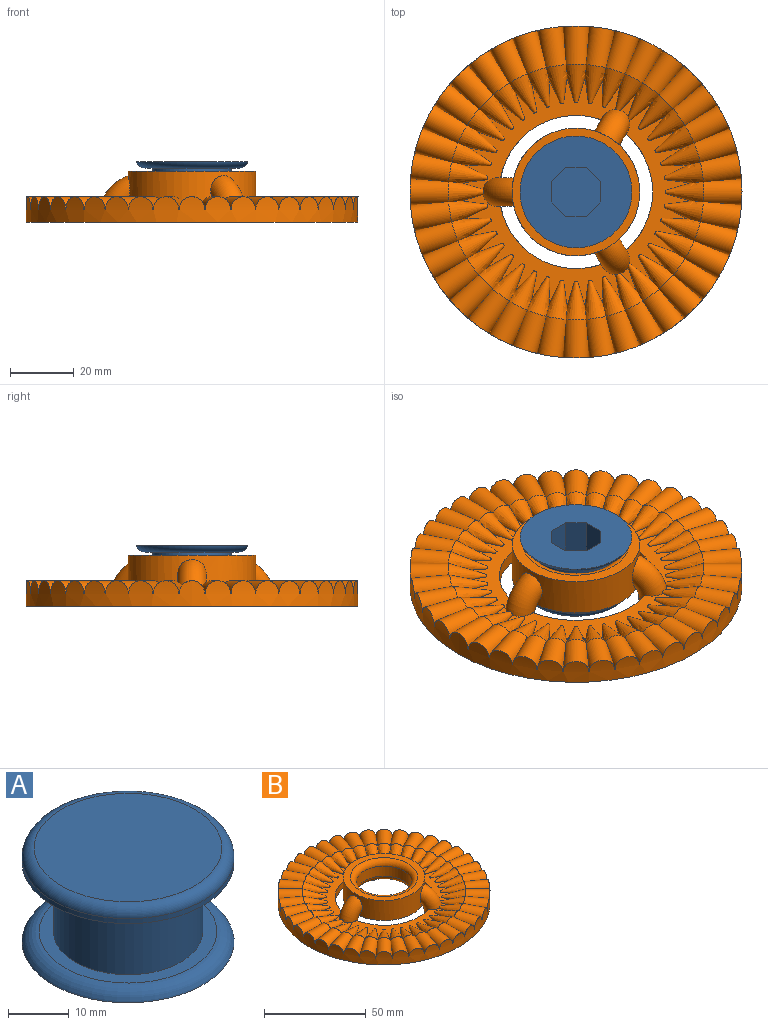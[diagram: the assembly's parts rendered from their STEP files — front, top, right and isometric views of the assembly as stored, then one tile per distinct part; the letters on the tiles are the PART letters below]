
ASSEMBLY  parts=2 mates=1
PART A: 17 faces, bbox 38.3x38.3x20 mm
  f0: plane 15x6.3mm, normal (-1,0,0), area 94.4mm2, adj f1,f7,f8,f16
  f1: plane 15x4.45mm, normal (-0.71,0.71,0), area 94.4mm2, adj f0,f2,f8,f16
  f2: plane 15x6.3mm, normal (0,1,0), area 94.4mm2, adj f1,f3,f8,f16
  f3: plane 15x4.45mm, normal (0.71,0.71,0), area 94.4mm2, adj f2,f4,f8,f16
  f4: plane 15x6.3mm, normal (1,0,0), area 94.4mm2, adj f3,f5,f8,f16
  f5: plane 15x4.45mm, normal (0.71,-0.71,0), area 94.4mm2, adj f4,f6,f8,f16
  f6: plane 15x6.3mm, normal (0,-1,0), area 94.4mm2, adj f5,f7,f8,f16
  f7: plane 15x4.45mm, normal (-0.71,-0.71,0), area 94.4mm2, adj f0,f6,f8,f16
  f8: plane 35x35mm, normal (0,0,-1), area 770.7mm2, adj f0,f1,f2,f3,f4,f5,f6,f7
  f9: plane 35x35mm, normal (0,0,-1), area 486.8mm2, adj f10,f14
  f10: cylinder r=12.3mm len=24.6mm, axis (0,0,-1), area 1082mm2, adj f9,f11
  f11: plane 29.34x29.34mm, normal (0,0,1), area 201mm2, adj f10,f15
  f12: plane 31x31mm, normal (0,0,1), area 754.8mm2, adj f13
  f13: torus R=15.5mm, axis (0,0,1), area 331.1mm2, adj f12,f14
  f14: cylinder r=17.5mm len=35mm, axis (0,0,1), area 110mm2, adj f9,f13
  f15: torus R=14.67mm, axis (0,0,-1), area 378.1mm2, adj f8,f11
  f16: plane 15.2x15.2mm, normal (0,0,-1), area 191.4mm2, adj f0,f1,f2,f3,f4,f5,f6,f7
PART B: 180 faces, bbox 20000000000000000038313501714693374724319102545303840223056070291987586484079775119224722902163606470656x20000000000000000038313501714693374724319102545303840223056070291987586484079775119224722902163606470656x16 mm
  f0: cylinder r=4mm len=13.1mm, axis (-0.16,0.99,0), area 111.7mm2, adj f1,f2,f175,f176,f177,f178
  f1: plane 1.02x0.16mm, normal (0,0,1), area 0.1mm2, adj f0,f2,f178
  f2: cylinder r=4mm len=12mm, axis (0,1,0), area 111.7mm2, adj f0,f1,f3,f4,f174,f178
  f3: plane 1.02x0.16mm, normal (0,0,1), area 0.1mm2, adj f2,f4,f178
  f4: cylinder r=4mm len=13.1mm, axis (0.16,0.99,0), area 111.7mm2, adj f2,f3,f5,f6,f173,f178
  f5: plane 1.01x0.32mm, normal (0,0,1), area 0.1mm2, adj f4,f6,f178
  f6: cylinder r=4mm len=13.89mm, axis (0.31,0.95,0), area 111.7mm2, adj f4,f5,f7,f8,f172,f178
  f7: plane 0.97x0.46mm, normal (0,0,1), area 0.1mm2, adj f6,f8,f178
  f8: cylinder r=4mm len=14.32mm, axis (0.45,0.89,0), area 111.7mm2, adj f6,f7,f9,f10,f171,f178
  f9: plane 0.91x0.6mm, normal (0,0,1), area 0.1mm2, adj f8,f10,f178
  f10: cylinder r=4mm len=14.41mm, axis (0.59,0.81,0), area 111.7mm2, adj f8,f9,f11,f12,f170,f178
  f11: plane 0.83x0.72mm, normal (0,0,1), area 0.1mm2, adj f10,f12,f178
  f12: cylinder r=4mm len=14.14mm, axis (0.71,0.71,0), area 111.7mm2, adj f10,f11,f13,f14,f169,f178
  f13: plane 0.83x0.72mm, normal (0,0,1), area 0.1mm2, adj f12,f14,f178
  f14: cylinder r=4mm len=14.41mm, axis (0.81,0.59,0), area 111.7mm2, adj f12,f13,f15,f16,f168,f178
  f15: plane 0.91x0.6mm, normal (0,0,1), area 0.1mm2, adj f14,f16,f178
  f16: cylinder r=4mm len=14.32mm, axis (0.89,0.45,0), area 111.7mm2, adj f14,f15,f17,f18,f167,f178
  f17: plane 0.97x0.46mm, normal (0,0,1), area 0.1mm2, adj f16,f18,f178
  f18: cylinder r=4mm len=13.89mm, axis (0.95,0.31,0), area 111.7mm2, adj f16,f17,f19,f20,f166,f178
  f19: plane 1.01x0.32mm, normal (0,0,1), area 0.1mm2, adj f18,f20,f178
  f20: cylinder r=4mm len=13.1mm, axis (0.99,0.16,0), area 111.7mm2, adj f18,f19,f21,f22,f165,f178
  f21: plane 1.02x0.16mm, normal (0,0,1), area 0.1mm2, adj f20,f22,f178
  f22: cylinder r=4mm len=12mm, axis (1,0,0), area 111.7mm2, adj f20,f21,f23,f24,f164,f178
  f23: plane 1.02x0.16mm, normal (0,0,1), area 0.1mm2, adj f22,f24,f178
  f24: cylinder r=4mm len=13.1mm, axis (0.99,-0.16,0), area 111.7mm2, adj f22,f23,f25,f26,f163,f178
  f25: plane 1.01x0.32mm, normal (0,0,1), area 0.1mm2, adj f24,f26,f178
  f26: cylinder r=4mm len=13.89mm, axis (0.95,-0.31,0), area 111.7mm2, adj f24,f25,f27,f28,f162,f178
  f27: plane 0.97x0.46mm, normal (0,0,1), area 0.1mm2, adj f26,f28,f178
  f28: cylinder r=4mm len=14.32mm, axis (0.89,-0.45,0), area 111.7mm2, adj f26,f27,f29,f30,f161,f178
  f29: plane 0.91x0.6mm, normal (0,0,1), area 0.1mm2, adj f28,f30,f178
  f30: cylinder r=4mm len=14.41mm, axis (0.81,-0.59,0), area 111.7mm2, adj f28,f29,f31,f32,f160,f178
  f31: plane 0.83x0.72mm, normal (0,0,1), area 0.1mm2, adj f30,f32,f178
  f32: cylinder r=4mm len=14.14mm, axis (0.71,-0.71,0), area 111.7mm2, adj f30,f31,f33,f34,f159,f178
  f33: plane 0.83x0.72mm, normal (0,0,1), area 0.1mm2, adj f32,f34,f178
  f34: cylinder r=4mm len=14.41mm, axis (0.59,-0.81,0), area 111.7mm2, adj f32,f33,f35,f36,f158,f178
  f35: plane 0.91x0.6mm, normal (0,0,1), area 0.1mm2, adj f34,f36,f178
  f36: cylinder r=4mm len=14.32mm, axis (0.45,-0.89,0), area 111.7mm2, adj f34,f35,f37,f38,f157,f178
  f37: plane 0.97x0.46mm, normal (0,0,1), area 0.1mm2, adj f36,f38,f178
  f38: cylinder r=4mm len=13.89mm, axis (0.31,-0.95,0), area 111.7mm2, adj f36,f37,f39,f40,f156,f178
  f39: plane 1.01x0.32mm, normal (0,0,1), area 0.1mm2, adj f38,f40,f178
  f40: cylinder r=4mm len=13.1mm, axis (0.16,-0.99,0), area 111.7mm2, adj f38,f39,f41,f42,f155,f178
  f41: plane 1.02x0.16mm, normal (0,0,1), area 0.1mm2, adj f40,f42,f178
  f42: cylinder r=4mm len=12mm, axis (0,-1,0), area 111.7mm2, adj f40,f41,f43,f44,f154,f178
  f43: plane 1.02x0.16mm, normal (0,0,1), area 0.1mm2, adj f42,f44,f178
  f44: cylinder r=4mm len=13.1mm, axis (-0.16,-0.99,0), area 111.7mm2, adj f42,f43,f45,f46,f153,f178
  f45: plane 1.01x0.32mm, normal (0,0,1), area 0.1mm2, adj f44,f46,f178
  f46: cylinder r=4mm len=13.89mm, axis (-0.31,-0.95,0), area 111.7mm2, adj f44,f45,f47,f48,f152,f178
  f47: plane 0.97x0.46mm, normal (0,0,1), area 0.1mm2, adj f46,f48,f178
  f48: cylinder r=4mm len=14.32mm, axis (-0.45,-0.89,0), area 111.7mm2, adj f46,f47,f49,f50,f151,f178
  f49: plane 0.91x0.6mm, normal (0,0,1), area 0.1mm2, adj f48,f50,f178
  f50: cylinder r=4mm len=14.41mm, axis (-0.59,-0.81,0), area 111.7mm2, adj f48,f49,f51,f52,f150,f178
  f51: plane 0.83x0.72mm, normal (0,0,1), area 0.1mm2, adj f50,f52,f178
  f52: cylinder r=4mm len=14.14mm, axis (-0.71,-0.71,0), area 111.7mm2, adj f50,f51,f53,f54,f149,f178
  f53: plane 0.83x0.72mm, normal (0,0,1), area 0.1mm2, adj f52,f54,f178
  f54: cylinder r=4mm len=14.41mm, axis (-0.81,-0.59,0), area 111.7mm2, adj f52,f53,f55,f56,f148,f178
  f55: plane 0.91x0.6mm, normal (0,0,1), area 0.1mm2, adj f54,f56,f178
  f56: cylinder r=4mm len=14.32mm, axis (-0.89,-0.45,0), area 111.7mm2, adj f54,f55,f57,f58,f147,f178
  f57: plane 0.97x0.46mm, normal (0,0,1), area 0.1mm2, adj f56,f58,f178
  f58: cylinder r=4mm len=13.89mm, axis (-0.95,-0.31,0), area 111.7mm2, adj f56,f57,f59,f60,f146,f178
  f59: plane 1.01x0.32mm, normal (0,0,1), area 0.1mm2, adj f58,f60,f178
  f60: cylinder r=4mm len=13.1mm, axis (-0.99,-0.16,0), area 111.7mm2, adj f58,f59,f61,f62,f145,f178
  f61: plane 1.02x0.16mm, normal (0,0,1), area 0.1mm2, adj f60,f62,f178
  f62: cylinder r=4mm len=12mm, axis (-1,0,0), area 111.7mm2, adj f60,f61,f63,f64,f144,f178
  f63: plane 1.02x0.16mm, normal (0,0,1), area 0.1mm2, adj f62,f64,f178
  f64: cylinder r=4mm len=13.1mm, axis (-0.99,0.16,0), area 111.7mm2, adj f62,f63,f65,f66,f143,f178
  f65: plane 1.01x0.32mm, normal (0,0,1), area 0.1mm2, adj f64,f66,f178
  f66: cylinder r=4mm len=13.89mm, axis (-0.95,0.31,0), area 111.7mm2, adj f64,f65,f67,f68,f142,f178
  f67: plane 0.97x0.46mm, normal (0,0,1), area 0.1mm2, adj f66,f68,f178
  f68: cylinder r=4mm len=14.32mm, axis (-0.89,0.45,0), area 111.7mm2, adj f66,f67,f69,f70,f141,f178
  f69: plane 0.91x0.6mm, normal (0,0,1), area 0.1mm2, adj f68,f70,f178
  f70: cylinder r=4mm len=14.41mm, axis (-0.81,0.59,0), area 111.7mm2, adj f68,f69,f71,f72,f140,f178
  f71: plane 0.83x0.72mm, normal (0,0,1), area 0.1mm2, adj f70,f72,f178
  f72: cylinder r=4mm len=14.14mm, axis (-0.71,0.71,0), area 111.7mm2, adj f70,f71,f73,f74,f139,f178
  f73: plane 0.83x0.72mm, normal (0,0,1), area 0.1mm2, adj f72,f74,f178
  f74: cylinder r=4mm len=14.41mm, axis (-0.59,0.81,0), area 111.7mm2, adj f72,f73,f75,f76,f138,f178
  f75: plane 0.91x0.6mm, normal (0,0,1), area 0.1mm2, adj f74,f76,f178
  f76: cylinder r=4mm len=14.32mm, axis (-0.45,0.89,0), area 111.7mm2, adj f74,f75,f77,f78,f176,f178
  f77: plane 0.97x0.46mm, normal (0,0,1), area 0.1mm2, adj f76,f176,f178
  f78: cone r=0.5mm half-angle=16.3deg, axis (0.45,-0.89,0), area 72.9mm2, adj f76,f79,f81,f136,f137,f138
  f79: cone r=0.5mm half-angle=16.3deg, axis (0.31,-0.95,0), area 74.6mm2, adj f78,f80,f81,f175,f176
  f80: plane 0.95x0.5mm, normal (-0.31,0.95,0), area 0.4mm2, adj f79,f81
  f81: plane 49.82x35.18mm, normal (0,0,1), area 360.6mm2, adj f78,f79,f80,f82,f124,f125,f126,f127
  f82: torus R=10mm, axis (0,1,0), area 250mm2, adj f81,f83,f108,f121,f122,f123,f124,f164
  f83: plane 40x39.94mm, normal (0,0,-1), area 398.9mm2, adj f82,f84,f104,f123,f136
  f84: torus R=10mm, axis (0.87,-0.5,0), area 244mm2, adj f83,f85,f86,f87,f100,f103,f108,f121
  f85: plane 7.24x4.91mm, normal (0,0,1), area 10.4mm2, adj f84,f150,f151
  f86: plane 0.49x0.3mm, normal (-0.59,-0.81,0), area 0.1mm2, adj f84,f87,f150
  f87: plane 54.92x20.39mm, normal (0,0,1), area 349.2mm2, adj f84,f86,f88,f89,f90,f91,f92,f93
  f88: plane 0.71x0.71mm, normal (-0.71,-0.71,0), area 0.4mm2, adj f87,f149
  f89: plane 0.81x0.59mm, normal (-0.81,-0.59,0), area 0.4mm2, adj f87,f148
  f90: plane 0.89x0.5mm, normal (-0.89,-0.45,0), area 0.4mm2, adj f87,f147
  f91: plane 0.95x0.5mm, normal (-0.95,-0.31,0), area 0.4mm2, adj f87,f146
  f92: plane 0.99x0.5mm, normal (-0.99,-0.16,0), area 0.4mm2, adj f87,f145
  f93: plane 1x0.5mm, normal (-1,0,0), area 0.4mm2, adj f87,f144
  f94: plane 0.99x0.5mm, normal (-0.99,0.16,0), area 0.4mm2, adj f87,f143
  f95: plane 0.95x0.5mm, normal (-0.95,0.31,0), area 0.4mm2, adj f87,f142
  f96: plane 0.89x0.5mm, normal (-0.89,0.45,0), area 0.4mm2, adj f87,f141
  f97: plane 0.81x0.59mm, normal (-0.81,0.59,0), area 0.4mm2, adj f87,f140
  f98: plane 0.71x0.71mm, normal (-0.71,0.71,0), area 0.4mm2, adj f87,f139
  f99: plane 0.49x0.3mm, normal (-0.59,0.81,0), area 0.1mm2, adj f87,f136,f138
  f100: cylinder r=24mm len=36.62mm, axis (0,0,-1), area 166.2mm2, adj f84,f87,f101,f102,f103,f136
  f101: plane 104x104mm, normal (0,0,-1), area 6750.5mm2, adj f100,f102,f103,f121,f122,f124,f178
  f102: cylinder r=4.5mm len=7.52mm, axis (0,0,1), area 11.3mm2, adj f100,f101,f124,f136
  f103: cylinder r=4.5mm len=7.52mm, axis (0,0,1), area 11.3mm2, adj f84,f100,f101,f121
  f104: torus R=16.5mm, axis (0,0,1), area 432mm2, adj f83,f105
  f105: cylinder r=13.5mm len=27mm, axis (0,0,-1), area 508.9mm2, adj f104,f106
  f106: torus R=16.5mm, axis (0,0,1), area 432mm2, adj f105,f107
  f107: plane 40x40mm, normal (0,0,1), area 401.3mm2, adj f106,f123
  f108: plane 49.82x35.18mm, normal (0,0,1), area 360.6mm2, adj f82,f84,f109,f110,f111,f112,f113,f114
  f109: plane 0.99x0.5mm, normal (0.99,-0.16,0), area 0.4mm2, adj f108,f163
  f110: plane 0.95x0.5mm, normal (0.95,-0.31,0), area 0.4mm2, adj f108,f162
  f111: plane 0.89x0.5mm, normal (0.89,-0.45,0), area 0.4mm2, adj f108,f161
  f112: plane 0.81x0.59mm, normal (0.81,-0.59,0), area 0.4mm2, adj f108,f160
  f113: plane 0.71x0.71mm, normal (0.71,-0.71,0), area 0.4mm2, adj f108,f159
  f114: plane 0.81x0.59mm, normal (0.59,-0.81,0), area 0.4mm2, adj f108,f158
  f115: plane 0.89x0.5mm, normal (0.45,-0.89,0), area 0.4mm2, adj f108,f157
  f116: plane 0.95x0.5mm, normal (0.31,-0.95,0), area 0.4mm2, adj f108,f156
  f117: plane 0.99x0.5mm, normal (0.16,-0.99,0), area 0.4mm2, adj f108,f155
  f118: plane 1x0.5mm, normal (0,-1,0), area 0.4mm2, adj f108,f154
  f119: plane 0.99x0.5mm, normal (-0.16,-0.99,0), area 0.4mm2, adj f108,f153
  f120: plane 0.95x0.5mm, normal (-0.31,-0.95,0), area 0.4mm2, adj f108,f152
  f121: cylinder r=24mm len=31.71mm, axis (0,0,-1), area 166.2mm2, adj f82,f84,f101,f103,f108,f122
  f122: cylinder r=4.5mm len=8.56mm, axis (0,0,1), area 11.3mm2, adj f82,f101,f121,f124
  f123: cylinder r=20mm len=40mm, axis (0,0,-1), area 1280.3mm2, adj f82,f83,f84,f107,f136
  f124: cylinder r=24mm len=31.71mm, axis (0,0,-1), area 166.2mm2, adj f81,f82,f101,f102,f122,f136
  f125: plane 0.99x0.5mm, normal (-0.16,0.99,0), area 0.4mm2, adj f81,f175
  f126: plane 1x0.5mm, normal (0,1,0), area 0.4mm2, adj f81,f174
  f127: plane 0.99x0.5mm, normal (0.16,0.99,0), area 0.4mm2, adj f81,f173
  f128: plane 0.95x0.5mm, normal (0.31,0.95,0), area 0.4mm2, adj f81,f172
  f129: plane 0.89x0.5mm, normal (0.45,0.89,0), area 0.4mm2, adj f81,f171
  f130: plane 0.81x0.59mm, normal (0.59,0.81,0), area 0.4mm2, adj f81,f170
  f131: plane 0.71x0.71mm, normal (0.71,0.71,0), area 0.4mm2, adj f81,f169
  f132: plane 0.81x0.59mm, normal (0.81,0.59,0), area 0.4mm2, adj f81,f168
  f133: plane 0.89x0.5mm, normal (0.89,0.45,0), area 0.4mm2, adj f81,f167
  f134: plane 0.95x0.5mm, normal (0.95,0.31,0), area 0.4mm2, adj f81,f166
  f135: plane 0.99x0.5mm, normal (0.99,0.16,0), area 0.4mm2, adj f81,f165
  f136: torus R=10mm, axis (-0.87,-0.5,0), area 249.6mm2, adj f78,f81,f83,f87,f99,f100,f102,f123
  f137: plane 7.24x4.91mm, normal (0,0,1), area 10.4mm2, adj f78,f136,f138
  f138: cone r=0.5mm half-angle=16.3deg, axis (0.59,-0.81,0), area 74.2mm2, adj f74,f78,f87,f99,f136,f137,f139
  f139: cone r=0.5mm half-angle=16.3deg, axis (0.71,-0.71,0), area 74.6mm2, adj f72,f87,f98,f138,f140
  f140: cone r=0.5mm half-angle=16.3deg, axis (0.81,-0.59,0), area 74.6mm2, adj f70,f87,f97,f139,f141
  f141: cone r=0.5mm half-angle=16.3deg, axis (0.89,-0.45,0), area 74.6mm2, adj f68,f87,f96,f140,f142
  f142: cone r=0.5mm half-angle=16.3deg, axis (0.95,-0.31,0), area 74.6mm2, adj f66,f87,f95,f141,f143
  f143: cone r=0.5mm half-angle=16.3deg, axis (0.99,-0.16,0), area 74.6mm2, adj f64,f87,f94,f142,f144
  f144: cone r=0.5mm half-angle=16.3deg, axis (1,0,0), area 74.6mm2, adj f62,f87,f93,f143,f145
  f145: cone r=0.5mm half-angle=16.3deg, axis (0.99,0.16,0), area 74.6mm2, adj f60,f87,f92,f144,f146
  f146: cone r=0.5mm half-angle=16.3deg, axis (0.95,0.31,0), area 74.6mm2, adj f58,f87,f91,f145,f147
  f147: cone r=0.5mm half-angle=16.3deg, axis (0.89,0.45,0), area 74.6mm2, adj f56,f87,f90,f146,f148
  f148: cone r=0.5mm half-angle=16.3deg, axis (0.81,0.59,0), area 74.6mm2, adj f54,f87,f89,f147,f149
  f149: cone r=0.5mm half-angle=16.3deg, axis (0.71,0.71,0), area 74.6mm2, adj f52,f87,f88,f148,f150
  f150: cone r=0.5mm half-angle=16.3deg, axis (0.59,0.81,0), area 74.2mm2, adj f50,f84,f85,f86,f87,f149,f151
  f151: cone r=0.5mm half-angle=16.3deg, axis (0.45,0.89,0), area 72.9mm2, adj f48,f84,f85,f108,f150,f152
  f152: cone r=0.5mm half-angle=16.3deg, axis (0.31,0.95,0), area 74.6mm2, adj f46,f108,f120,f151,f153
  f153: cone r=0.5mm half-angle=16.3deg, axis (0.16,0.99,0), area 74.6mm2, adj f44,f108,f119,f152,f154
  f154: cone r=0.5mm half-angle=16.3deg, axis (0,1,0), area 74.6mm2, adj f42,f108,f118,f153,f155
  f155: cone r=0.5mm half-angle=16.3deg, axis (-0.16,0.99,0), area 74.6mm2, adj f40,f108,f117,f154,f156
  f156: cone r=0.5mm half-angle=16.3deg, axis (-0.31,0.95,0), area 74.6mm2, adj f38,f108,f116,f155,f157
  f157: cone r=0.5mm half-angle=16.3deg, axis (-0.45,0.89,0), area 74.6mm2, adj f36,f108,f115,f156,f158
  f158: cone r=0.5mm half-angle=16.3deg, axis (-0.59,0.81,0), area 74.6mm2, adj f34,f108,f114,f157,f159
  f159: cone r=0.5mm half-angle=16.3deg, axis (-0.71,0.71,0), area 74.6mm2, adj f32,f108,f113,f158,f160
  f160: cone r=0.5mm half-angle=16.3deg, axis (-0.81,0.59,0), area 74.6mm2, adj f30,f108,f112,f159,f161
  f161: cone r=0.5mm half-angle=16.3deg, axis (-0.89,0.45,0), area 74.6mm2, adj f28,f108,f111,f160,f162
  f162: cone r=0.5mm half-angle=16.3deg, axis (-0.95,0.31,0), area 74.6mm2, adj f26,f108,f110,f161,f163
  f163: cone r=0.5mm half-angle=16.3deg, axis (-0.99,0.16,0), area 74.6mm2, adj f24,f108,f109,f162,f164
  f164: cone r=0.5mm half-angle=16.3deg, axis (-1,0,0), area 72.4mm2, adj f22,f81,f82,f108,f163,f165
  f165: cone r=0.5mm half-angle=16.3deg, axis (-0.99,-0.16,0), area 74.6mm2, adj f20,f81,f135,f164,f166
  f166: cone r=0.5mm half-angle=16.3deg, axis (-0.95,-0.31,0), area 74.6mm2, adj f18,f81,f134,f165,f167
  f167: cone r=0.5mm half-angle=16.3deg, axis (-0.89,-0.45,0), area 74.6mm2, adj f16,f81,f133,f166,f168
  f168: cone r=0.5mm half-angle=16.3deg, axis (-0.81,-0.59,0), area 74.6mm2, adj f14,f81,f132,f167,f169
  f169: cone r=0.5mm half-angle=16.3deg, axis (-0.71,-0.71,0), area 74.6mm2, adj f12,f81,f131,f168,f170
  f170: cone r=0.5mm half-angle=16.3deg, axis (-0.59,-0.81,0), area 74.6mm2, adj f10,f81,f130,f169,f171
  f171: cone r=0.5mm half-angle=16.3deg, axis (-0.45,-0.89,0), area 74.6mm2, adj f8,f81,f129,f170,f172
  f172: cone r=0.5mm half-angle=16.3deg, axis (-0.31,-0.95,0), area 74.6mm2, adj f6,f81,f128,f171,f173
  f173: cone r=0.5mm half-angle=16.3deg, axis (-0.16,-0.99,0), area 74.6mm2, adj f4,f81,f127,f172,f174
  f174: cone r=0.5mm half-angle=16.3deg, axis (0,-1,0), area 74.6mm2, adj f2,f81,f126,f173,f175
  f175: cone r=0.5mm half-angle=16.3deg, axis (0.16,-0.99,0), area 74.6mm2, adj f0,f79,f81,f125,f174
  f176: cylinder r=4mm len=13.89mm, axis (-0.31,0.95,0), area 111.7mm2, adj f0,f76,f77,f79,f177,f178
  f177: plane 1.01x0.32mm, normal (0,0,1), area 0.1mm2, adj f0,f176,f178
  f178: cylinder r=52mm len=104mm, axis (0,0,-1), area 2309.6mm2, adj f0,f1,f2,f3,f4,f5,f6,f7
  f179: plane 20000000000000000038313501714693374724319102545303840223056070291987586484079775119224722902163606470656x20000000000000000038313501714693374724319102545303840223056070291987586484079775119224722902163606470656mm, normal (0,0,-1), area 80000000000000007282879924029474800836836319614038924572363658998727223162810673217233440780332897524514816mm2
PLACE A rot(axis=(1,0,0),180deg) t=(52.45,24.14,-27.88)mm
PLACE B rot(axis=(-0.3,0.26,0.92),0deg) t=(52.45,24.14,-25.88)mm
MATE revolute A.f10 <-> B.f123  axis (0,0,1) through (52.45,24.14,-26.88)mm
